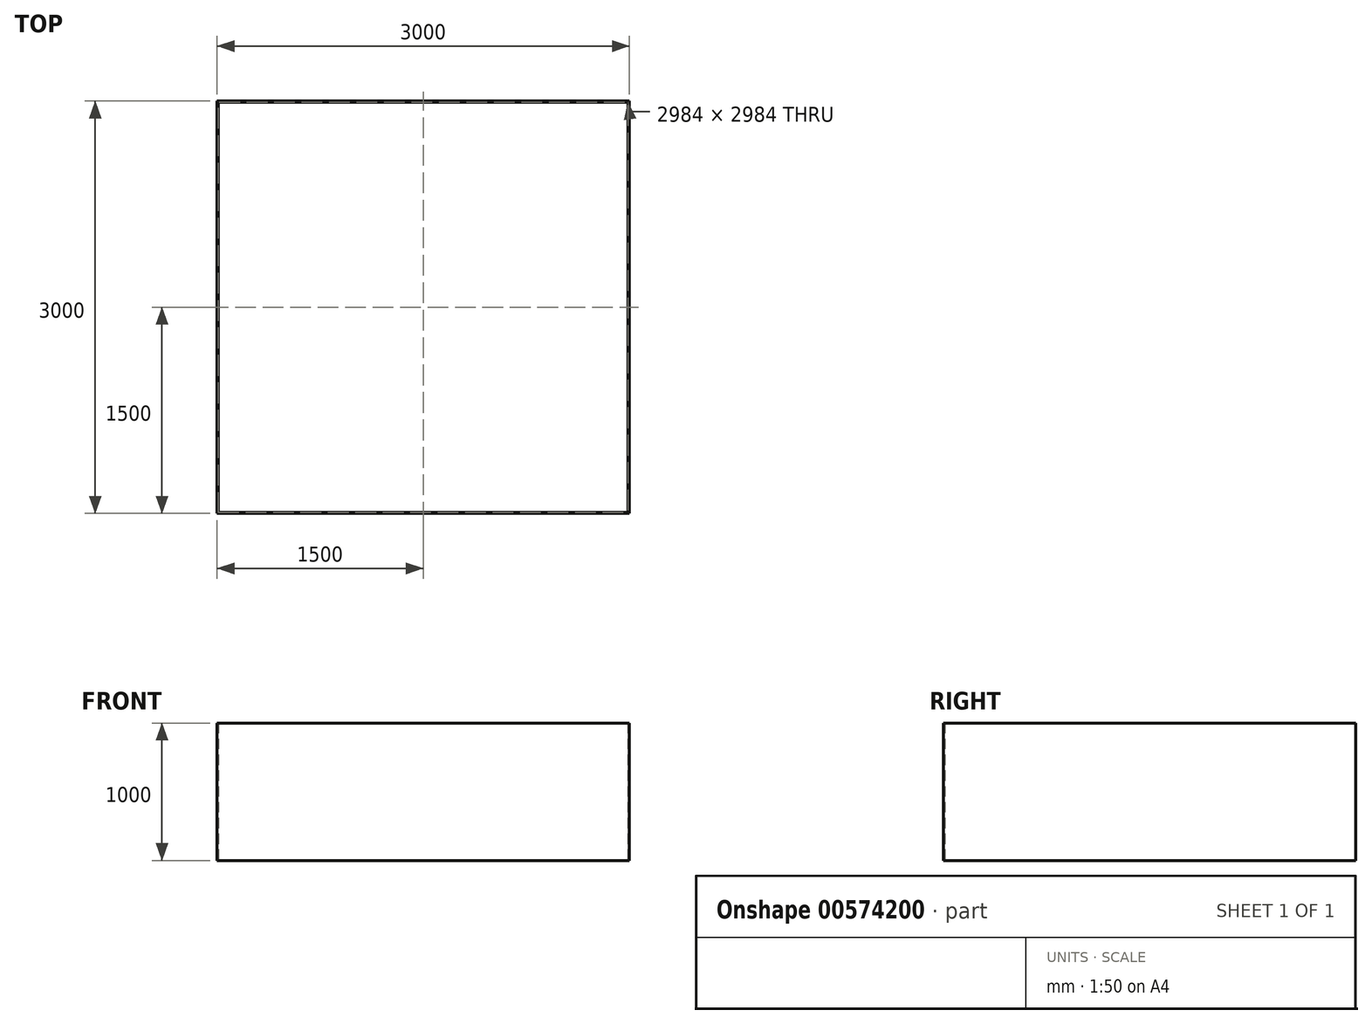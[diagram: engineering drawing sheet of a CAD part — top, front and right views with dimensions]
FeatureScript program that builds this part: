
annotation { "Feature Type Name" : "Feature", "Feature Type Description" : "" }
export const myFeature = defineFeature(function(context is Context, id is Id, definition is map)
    precondition{}
    {
        {
            var Q0;
            Q0=qCreatedBy(makeId("Top.planeOp"),FACE);
            var sketch = newSketch(context, id + "F0", { "sketchPlane" : qUnion([Q0])});
            skLineSegment(sketch, "E0.bottom", {"start": v(0, 0) * mm, "end": v(3000, 0) * mm});
            skLineSegment(sketch, "E0.top", {"start": v(0, 3000) * mm, "end": v(3000, 3000) * mm});
            skLineSegment(sketch, "E0.left", {"start": v(0, 0) * mm, "end": v(0, 3000) * mm});
            skLineSegment(sketch, "E0.right", {"start": v(3000, 0) * mm, "end": v(3000, 3000) * mm});
            skLineSegment(sketch, "E1.0", {"start": v(2992, 8) * mm, "end": v(2992, 2992) * mm});
            skLineSegment(sketch, "E1.1", {"start": v(8, 8) * mm, "end": v(2992, 8) * mm});
            skLineSegment(sketch, "E1.2", {"start": v(8, 8) * mm, "end": v(8, 2992) * mm});
            skLineSegment(sketch, "E1.3", {"start": v(8, 2992) * mm, "end": v(2992, 2992) * mm});
            skSolve(sketch);
        }
        {
            var Q0;
            Q0 = qSketchRegion(id + "F0", true);
            extrude(context, id + "F1", {"entities" : qUnion([Q0]), "depth" : 1000 * mm, "offsetDistance" : 25 * mm});
        }
    });
